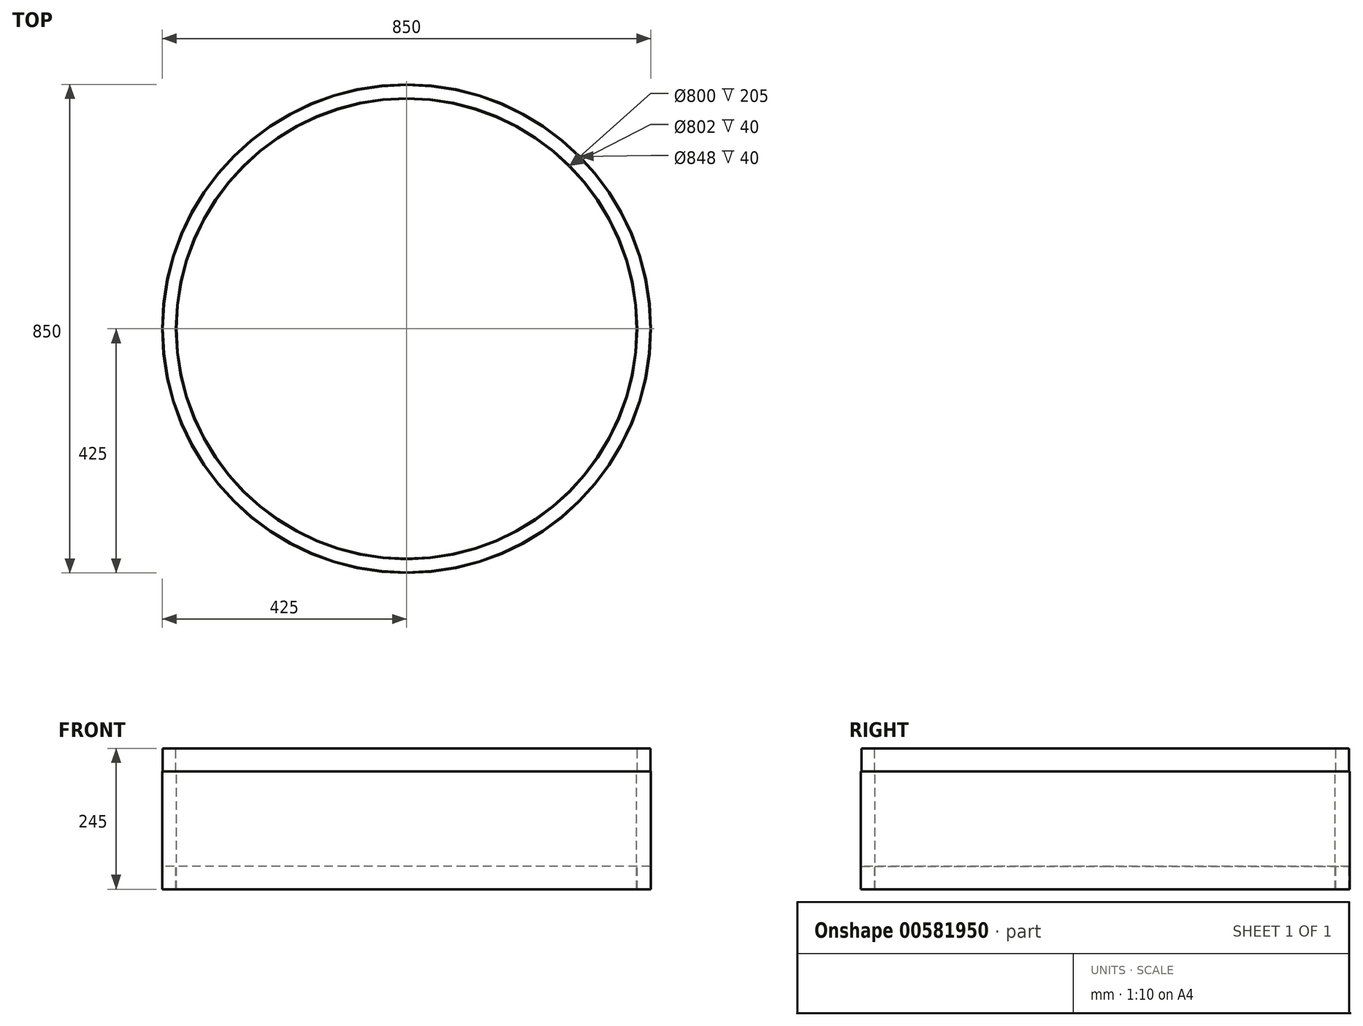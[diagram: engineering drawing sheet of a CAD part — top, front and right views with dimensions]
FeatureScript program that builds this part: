
annotation { "Feature Type Name" : "Feature", "Feature Type Description" : "" }
export const myFeature = defineFeature(function(context is Context, id is Id, definition is map)
    precondition{}
    {
        {
            var Q0;
            Q0=qCreatedBy(makeId("Front.planeOp"),FACE);
            var sketch = newSketch(context, id + "F0", { "sketchPlane" : qUnion([Q0])});
            skLineSegment(sketch, "E0", {"start": v(0, 345.75) * mm, "end": v(0, -558.03) * mm, "construction": true});
            skLineSegment(sketch, "E1", {"start": v(-400, -518.84) * mm, "end": v(-400, -313.84) * mm});
            skLineSegment(sketch, "E2", {"start": v(-400, -313.84) * mm, "end": v(-401, -313.84) * mm});
            skLineSegment(sketch, "E3", {"start": v(-401, -313.84) * mm, "end": v(-401, -273.84) * mm});
            skLineSegment(sketch, "E4", {"start": v(-401, -273.84) * mm, "end": v(-424, -273.84) * mm});
            skLineSegment(sketch, "E5", {"start": v(-424, -273.84) * mm, "end": v(-424, -313.84) * mm});
            skLineSegment(sketch, "E6", {"start": v(-424, -313.84) * mm, "end": v(-425, -313.84) * mm});
            skLineSegment(sketch, "E7", {"start": v(-425, -313.84) * mm, "end": v(-425, -518.84) * mm});
            skLineSegment(sketch, "E8", {"start": v(-425, -518.84) * mm, "end": v(-424, -518.84) * mm});
            skLineSegment(sketch, "E9", {"start": v(-424, -518.84) * mm, "end": v(-424, -478.84) * mm});
            skLineSegment(sketch, "E10", {"start": v(-424, -478.84) * mm, "end": v(-401, -478.84) * mm});
            skLineSegment(sketch, "E11", {"start": v(-401, -478.84) * mm, "end": v(-401, -518.84) * mm});
            skLineSegment(sketch, "E12", {"start": v(-401, -518.84) * mm, "end": v(-400, -518.84) * mm});
            skSolve(sketch);
        }
        {
            var Q0;
            Q0=qSketchRegion(id+"F0",true);
            var Q1;
            Q1=sQuery(id+"F0.wireOp",EDGE,"E0");
            revolve(context, id + "F1", {"entities" : qUnion([Q0]), "axis" : qUnion([Q1]), "revolveType" : RevolveType.FULL});
        }
    });
